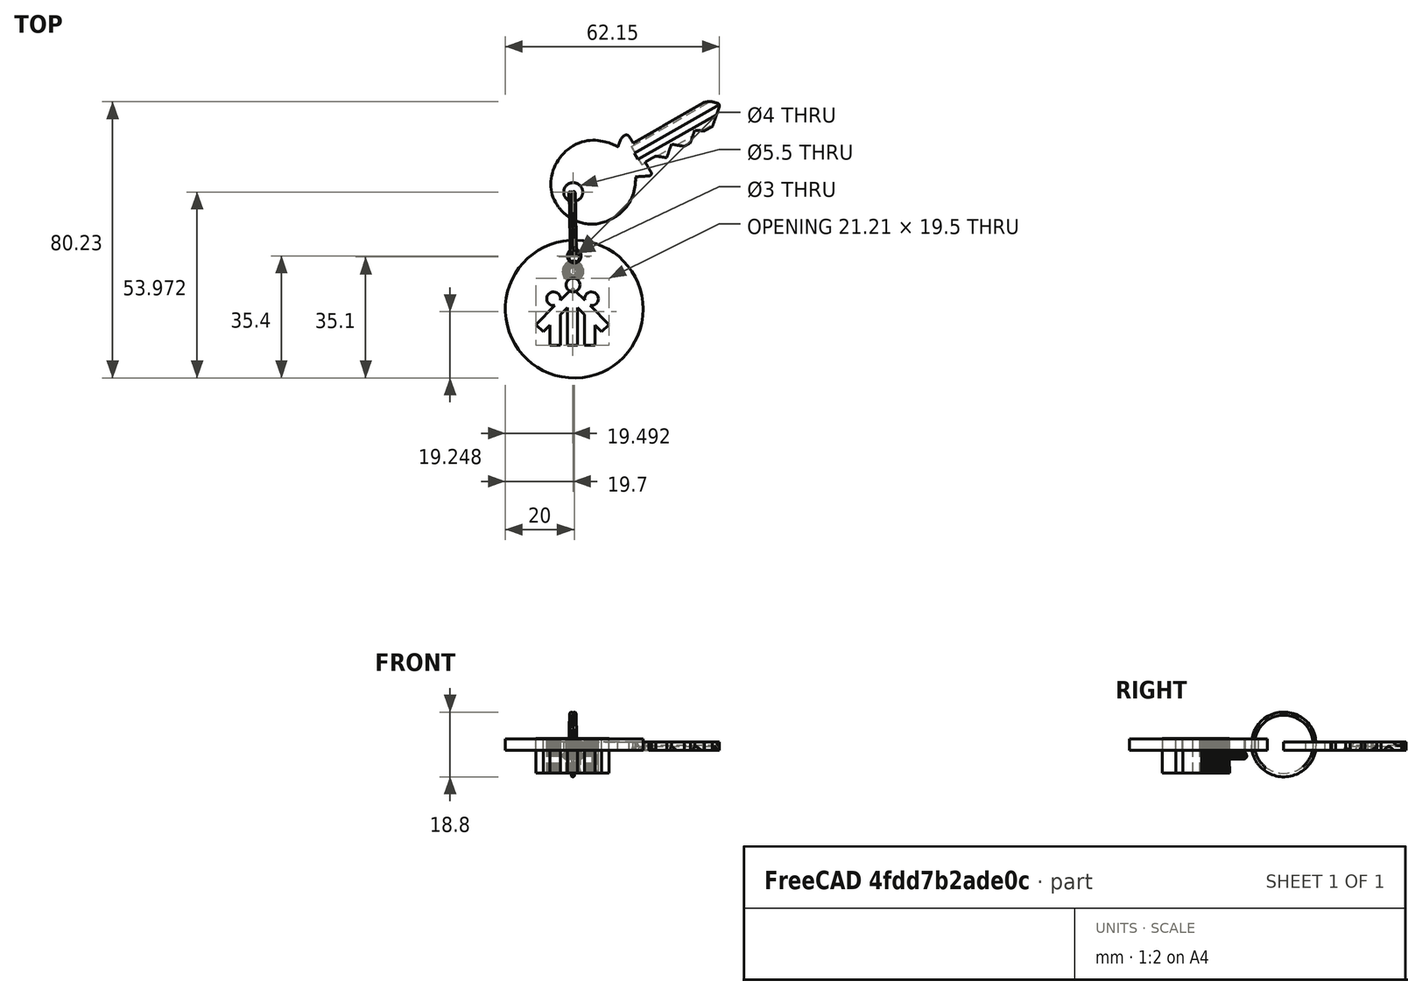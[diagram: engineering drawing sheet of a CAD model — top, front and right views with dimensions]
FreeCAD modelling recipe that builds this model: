
FCSTD DOCUMENT  (FreeCAD 0.18R16093 (Git))
Label: llavero_colegio
License: CreativeCommons Attribution-ShareAlike
LicenseURL: http://creativecommons.org/licenses/by-sa/4.0/
objects: Part::Feature×5, Part::Cylinder×2, App::DocumentObjectGroup×2, Part::Cut×2, Sketcher::SketchObject×1, PartDesign::Pocket×1, Mesh::Feature×1
note: 12 computed .brp shape members not serialized (recipe doc carries the construction recipe); baked Part::Feature solids carry a one-line shape summary decoded from their .brp

FEATURE [Part::Cylinder] Cylinder  label="casino-chip-main body"
  Angle = 360
  AttacherType = Attacher::AttachEngine3D
  Height = 3.3
  Radius = 20
FEATURE [Sketcher::SketchObject] Sketch  label="hole-sketch"
  MapMode = 5
  Placement = pos=(0,0,3.3) rot=(0,0,1;0rad)
  Support = -> [Cylinder]
  sketch-geometry (1):
    g0: Circle CenterX=0 CenterY=15.1 CenterZ=0 NormalX=0 NormalY=0 NormalZ=1 AngleXU=0 Radius=1.5
  constraints (3):
    c: Radius(g0) = 1.5
    c: PointOnObject(g0,g-2)
    c: DistanceY(g-1,g0) = 15.1
FEATURE [PartDesign::Pocket] Pocket  label="casino-chip-key-chain"
  Length = 5
  Length2 = 100
  Profile = -> Sketch
  Type = 1
FEATURE [App::DocumentObjectGroup] Group001  label="Casino-chip-src"
  Group = -> [Pocket]
FEATURE [Part::Feature] Sweep  label="key-ring-model-1"
  Placement = pos=(-1.2,24.7546,1.6391) rot=(0.333333,0.881918,0.333333;1.69612rad)
  shape: bbox 3.31 x 27.02 x 26.33 mm, 4 faces (baked)
FEATURE [Part::Feature] Cut  label="key-model-1"
  Placement = pos=(-5.46976,31.0266,0) rot=(0,0,1;0.517888rad)
  shape: bbox 49.82 x 36.6 x 2.3 mm, 44 faces (baked)
FEATURE [App::DocumentObjectGroup] Group  label="Assembly"
  Group = -> [Sweep,Cut]
FEATURE [Mesh::Feature] logo_maux_1_001  label="logo_maux_1.001"
  Placement = pos=(-2,-10,3.4) rot=(1,0,0;4.71239rad)
FEATURE [Part::Feature] logo_maux_1_001001
  shape: bbox 21.21 x 24.5 x 10 mm, 1690 faces, 0 solids (baked)
FEATURE [Part::Feature] logo_maux_1_001001_solid  label="logo_maux_1_001001 (Solid)"
  shape: bbox 21.21 x 24.5 x 10 mm, 1690 faces (baked)
FEATURE [Part::Feature] logo_maux_1_001001_solid001  label="logo_maux_1_001001 (Solid)001"
  shape: bbox 21.21 x 24.5 x 10 mm, 1413 faces (baked)
FEATURE [Part::Cut] Cut001
  Base = -> Cylinder
  Tool = -> logo_maux_1_001001_solid001
FEATURE [Part::Cylinder] Cylinder001  label="Cilindro"
  Angle = 360
  AttacherType = Attacher::AttachEngine3D
  Height = 10
  Placement = pos=(0,15.4,-3) rot=(0,0,1;0rad)
  Radius = 2
FEATURE [Part::Cut] Cut002
  Base = -> Cut001
  Tool = -> Cylinder001
